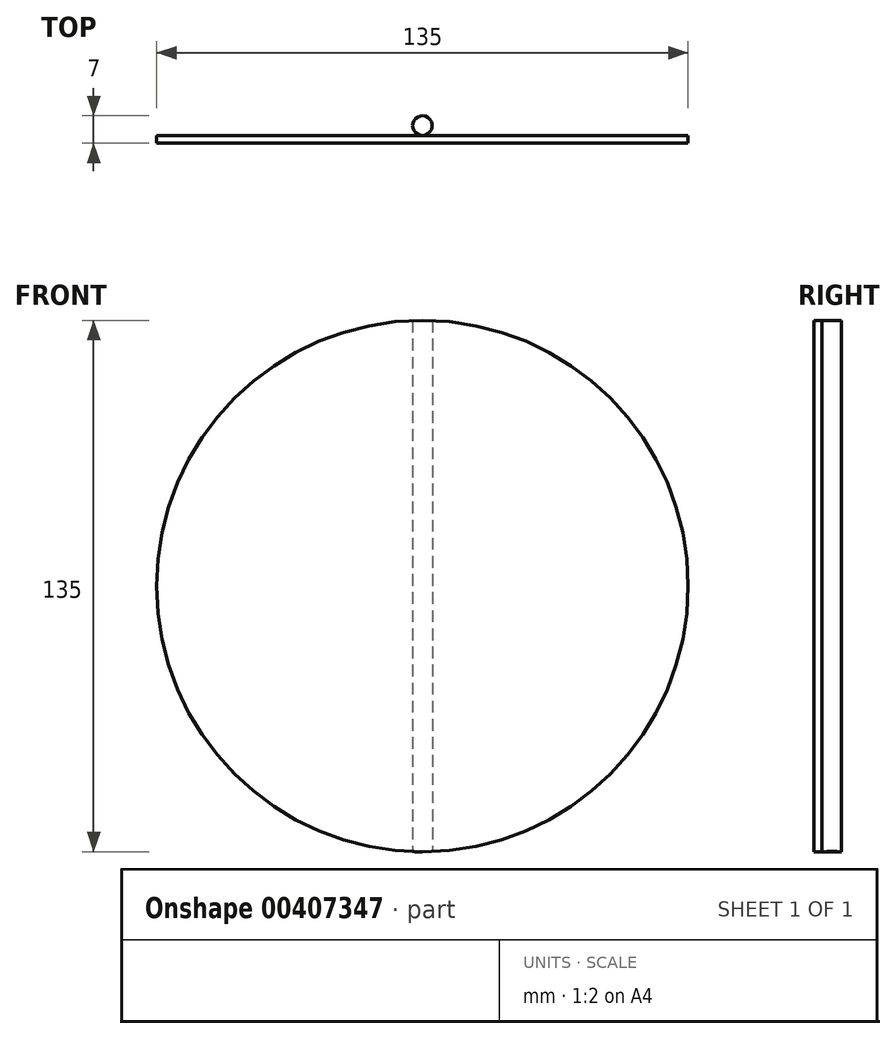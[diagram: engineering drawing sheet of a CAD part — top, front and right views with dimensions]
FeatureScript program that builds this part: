
annotation { "Feature Type Name" : "Feature", "Feature Type Description" : "" }
export const myFeature = defineFeature(function(context is Context, id is Id, definition is map)
    precondition{}
    {
        {
            var Q0;
            Q0=qCreatedBy(makeId("Front.planeOp"),FACE);
            var sketch = newSketch(context, id + "F0", { "sketchPlane" : qUnion([Q0])});
            skCircle(sketch, "E0", {"center": v(0, 0) * mm, "radius": 67.5 * mm});
            skSolve(sketch);
        }
        {
            var Q0;
            Q0 = qSketchRegion(id + "F0", true);
            extrude(context, id + "F1", {"entities" : qUnion([Q0]), "depth" : 2 * mm});
        }
        {
            var Q0;
            Q0=qCreatedBy(makeId("Top.planeOp"),FACE);
            var sketch = newSketch(context, id + "F2", { "sketchPlane" : qUnion([Q0])});
            skCircle(sketch, "E1", {"center": v(0, 2.5) * mm, "radius": 2.5 * mm});
            skSolve(sketch);
        }
        {
            var Q0;
            Q0 = qSketchRegion(id + "F2", true);
            extrude(context, id + "F3", {"entities" : qUnion([Q0]), "depth" : 100 * mm, "hasSecondDirection" : true, "secondDirectionOppositeDirection" : true, "secondDirectionDepth" : ((135 / 2) + 10) * mm});
        }
        {
            var Q0;
            Q0=makeQuery(id+"F3.opExtrude","SWEPT_BODY",BODY,{"disambiguationData":[OSD([sQuery(id+"F2.wireOp",EDGE,"E1")])]});
            deleteBodies(context, id + "F4", {"entities" : qUnion([Q0])});
        }
        {
            var Q0;
            Q0=makeQuery(id+"F2.imprint","IMPRINT",FACE,{"disambiguationData":[TD([[makeQuery(id+"F2.imprint","IMPRINT",EDGE,{"derivedFrom":sQuery(id+"F2.wireOp",EDGE,"E1")}),1.0]])]});
            var Q1;
            Q1 = qConstructionFilter(qBodyType(qCreatedBy(id + "F2" ,EDGE), BodyType.WIRE), ConstructionObject.NO);
            var Q2;
            Q2=makeQuery(id+"F1.opExtrude","SWEPT_FACE",FACE,{"disambiguationData":[OSD([sQuery(id+"F0.wireOp",EDGE,"E0")])]});
            var Q3;
            Q3=makeQuery(id+"F1.opExtrude","SWEPT_FACE",FACE,{"disambiguationData":[OSD([sQuery(id+"F0.wireOp",EDGE,"E0")])]});
            extrude(context, id + "F5", {"entities" : qUnion([Q0]), "operationType" : NewBodyOperationType.ADD, "surfaceEntities" : qUnion([Q1]), "endBound" : BoundingType.UP_TO_SURFACE, "endBoundEntityFace" : qUnion([Q2]), "depth" : (135 / 2) * mm, "hasSecondDirection" : true, "secondDirectionBound" : SecondDirectionBoundingType.UP_TO_SURFACE, "secondDirectionOppositeDirection" : true, "secondDirectionBoundEntityFace" : qUnion([Q3]), "secondDirectionDepth" : (135 / 2) * mm});
        }
    });
